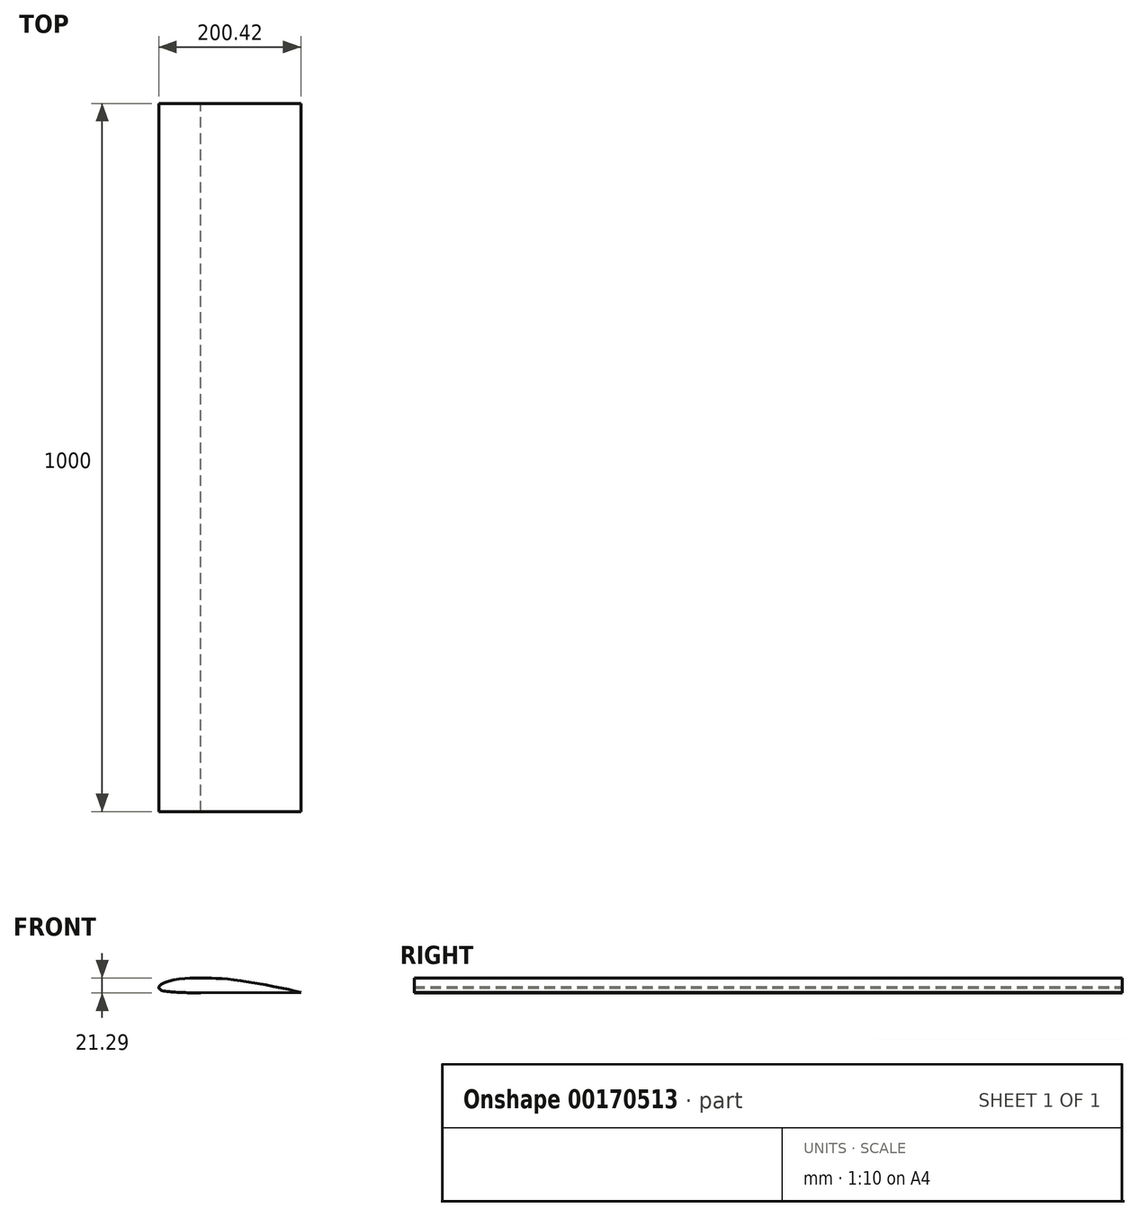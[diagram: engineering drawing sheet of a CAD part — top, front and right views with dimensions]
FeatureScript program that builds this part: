
annotation { "Feature Type Name" : "Feature", "Feature Type Description" : "" }
export const myFeature = defineFeature(function(context is Context, id is Id, definition is map)
    precondition{}
    {
        {
            var Q0;
            Q0=qCreatedBy(makeId("Front.planeOp"),FACE);
            var sketch = newSketch(context, id + "F0", { "sketchPlane" : qUnion([Q0])});
            skFitSpline(sketch, "E0", {"points": [v(-124.07, -4.39) * mm, v(-121.95, -2.37) * mm, v(-116.93, 0.6) * mm, v(-109.97, 3.36) * mm, v(-99.65, 5.55) * mm, v(-87.16, 6.72) * mm, v(-76, 7.39) * mm, v(-52.6, 7.39) * mm, v(-42.36, 7.02) * mm, v(-29.2, 6.03) * mm, v(-13.58, 4.36) * mm, v(13.17, -0.08) * mm, v(39.06, -4.71) * mm, v(60.3, -9.14) * mm, v(76.17, -12.73) * mm], "startDerivative": vector(68.98, 63.64) * mm, "endDerivative": vector(197.81, -45.26) * mm});
            skFitSpline(sketch, "E1", {"points": [v(-124.25, -6.68) * mm, v(-122.83, -8.33) * mm, v(-119.64, -10.2) * mm, v(-112.96, -11.34) * mm, v(-107.23, -12) * mm, v(-94.79, -12.93) * mm, v(-84.2, -13.24) * mm, v(-65.2, -13.78) * mm], "startDerivative": vector(16.84, -21.9) * mm, "endDerivative": vector(92.8, -2.85) * mm});
            skLineSegment(sketch, "E2", {"start": v(-65.2, -13.78) * mm, "end": v(76.17, -12.73) * mm});
            skLineSegment(sketch, "E3", {"start": v(-124.07, -4.39) * mm, "end": v(-124.25, -6.68) * mm});
            skFitSpline(sketch, "E4", {"points": [v(-365.7, -588) * mm, v(-357.42, -599.2) * mm, v(-275.81, -613.28) * mm, v(-79.86, -607.06) * mm, v(87.09, -595.05) * mm, v(-160.23, -567.3) * mm, v(-302.74, -568.53) * mm, v(-365.7, -588) * mm]});
            skSolve(sketch);
        }
        {
            var Q0;
            Q0=makeQuery(id+"F0.imprint","IMPRINT",FACE,{"disambiguationData":[TD([[makeQuery(id+"F0.imprint","IMPRINT",EDGE,{"derivedFrom":sQuery(id+"F0.wireOp",EDGE,"E0")}),-1.0]])]});
            var Q1;
            Q1 = qSketchRegion(id + "FvJIEPNwiPJHEdo_1", true);
            extrude(context, id + "F1", {"entities" : qUnion([Q0, Q1]), "depth" : 1000 * mm});
        }
    });
